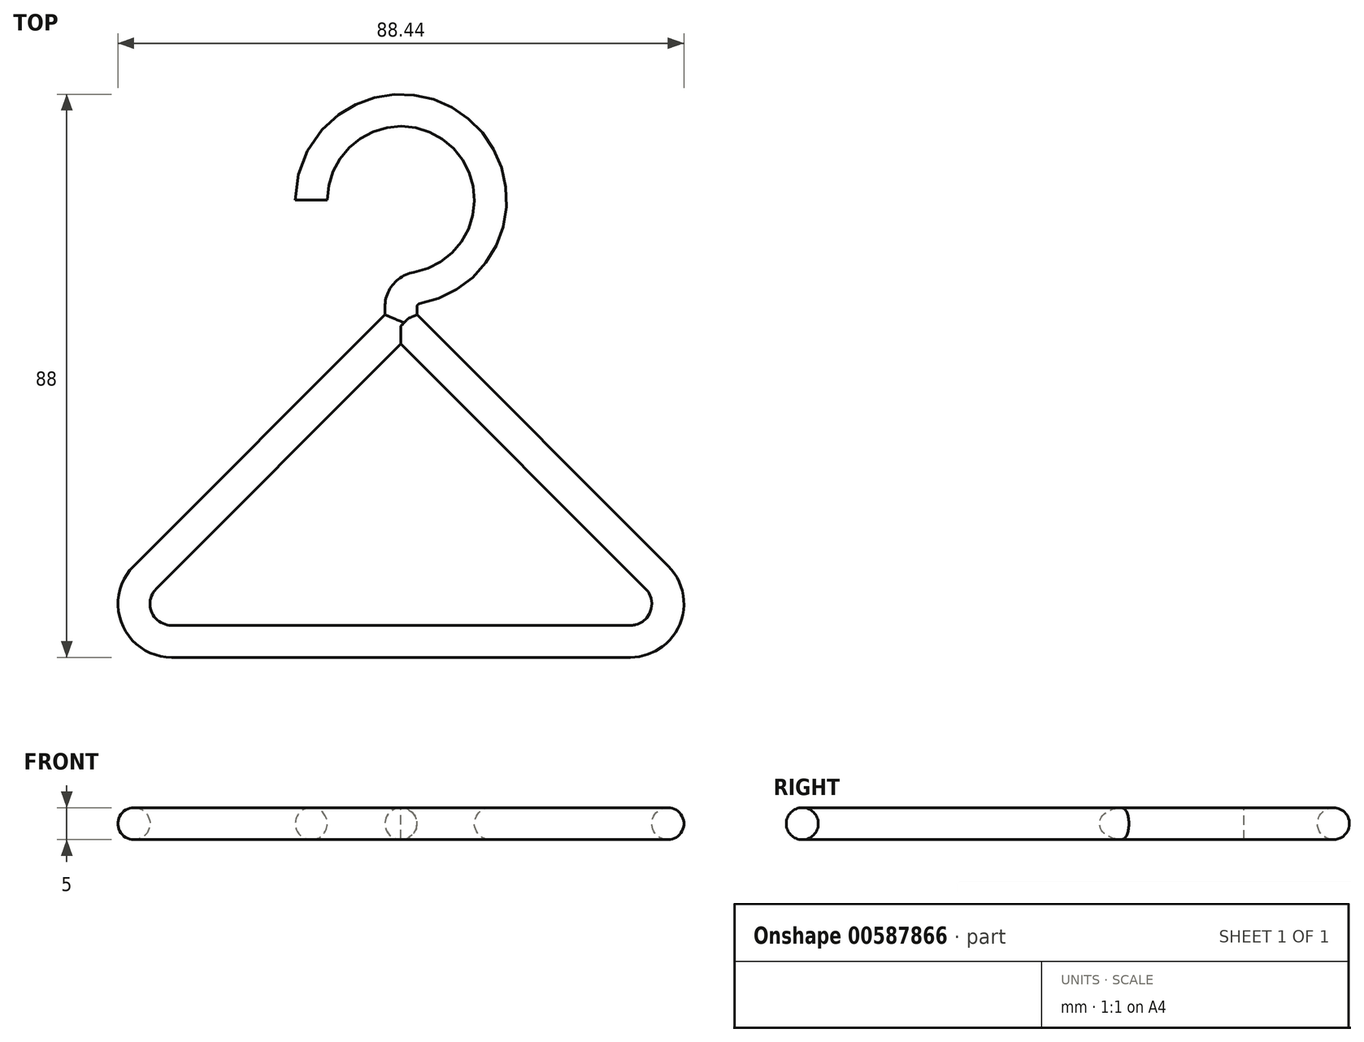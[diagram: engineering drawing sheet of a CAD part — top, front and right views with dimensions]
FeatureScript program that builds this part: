
annotation { "Feature Type Name" : "Feature", "Feature Type Description" : "" }
export const myFeature = defineFeature(function(context is Context, id is Id, definition is map)
    precondition{}
    {
        {
            var Q0;
            Q0=qCreatedBy(makeId("Top.planeOp"),FACE);
            var sketch = newSketch(context, id + "F0", { "sketchPlane" : qUnion([Q0])});
            skArc(sketch, "E0", {"start": v(-14, 0) * mm, "mid": v(8.98, 10.74) * mm, "end": v(2.47, -13.78) * mm});
            skLineSegment(sketch, "E1", {"start": v(0, -16.73) * mm, "end": v(0, -19) * mm});
            skLineSegment(sketch, "E2", {"start": v(0, -19) * mm, "end": v(40, -59) * mm, "construction": true});
            skLineSegment(sketch, "E3", {"start": v(-40, -59) * mm, "end": v(0, -19) * mm});
            skLineSegment(sketch, "E4", {"start": v(40, -59) * mm, "end": v(0.35, -19.35) * mm});
            skLineSegment(sketch, "E5", {"start": v(-35.86, -69) * mm, "end": v(35.86, -69) * mm});
            skArc(sketch, "E6", {"start": v(-40, -59) * mm, "mid": v(-41.27, -65.38) * mm, "end": v(-35.86, -69) * mm});
            skArc(sketch, "E7", {"start": v(35.86, -69) * mm, "mid": v(41.27, -65.38) * mm, "end": v(40, -59) * mm});
            skPoint(sketch, "E8.visualSharp", {"position": v(0, -14) * mm});
            skArc(sketch, "E8.filletArc", {"start": v(2.47, -13.78) * mm, "mid": v(0.7, -14.8) * mm, "end": v(0, -16.73) * mm});
            skSolve(sketch);
        }
        {
            var Q0;
            Q0=qCreatedBy(makeId("Front.planeOp"),FACE);
            var sketch = newSketch(context, id + "F1", { "sketchPlane" : qUnion([Q0])});
            skCircle(sketch, "E9", {"center": v(-14, 0) * mm, "radius": 2.5 * mm});
            skSolve(sketch);
        }
        {
            var Q0;
            Q0=makeQuery(id+"F1.imprint","IMPRINT",FACE,{"disambiguationData":[TD([[makeQuery(id+"F1.imprint","IMPRINT",EDGE,{"derivedFrom":sQuery(id+"F1.wireOp",EDGE,"E9")}),1.0]])]});
            var Q1;
            Q1 = qConstructionFilter(qBodyType(qCreatedBy(id + "F0" ,EDGE), BodyType.WIRE), ConstructionObject.NO);
            sweep(context, id + "F2", {"profiles" : qUnion([Q0]), "path" : qUnion([Q1])});
        }
    });
